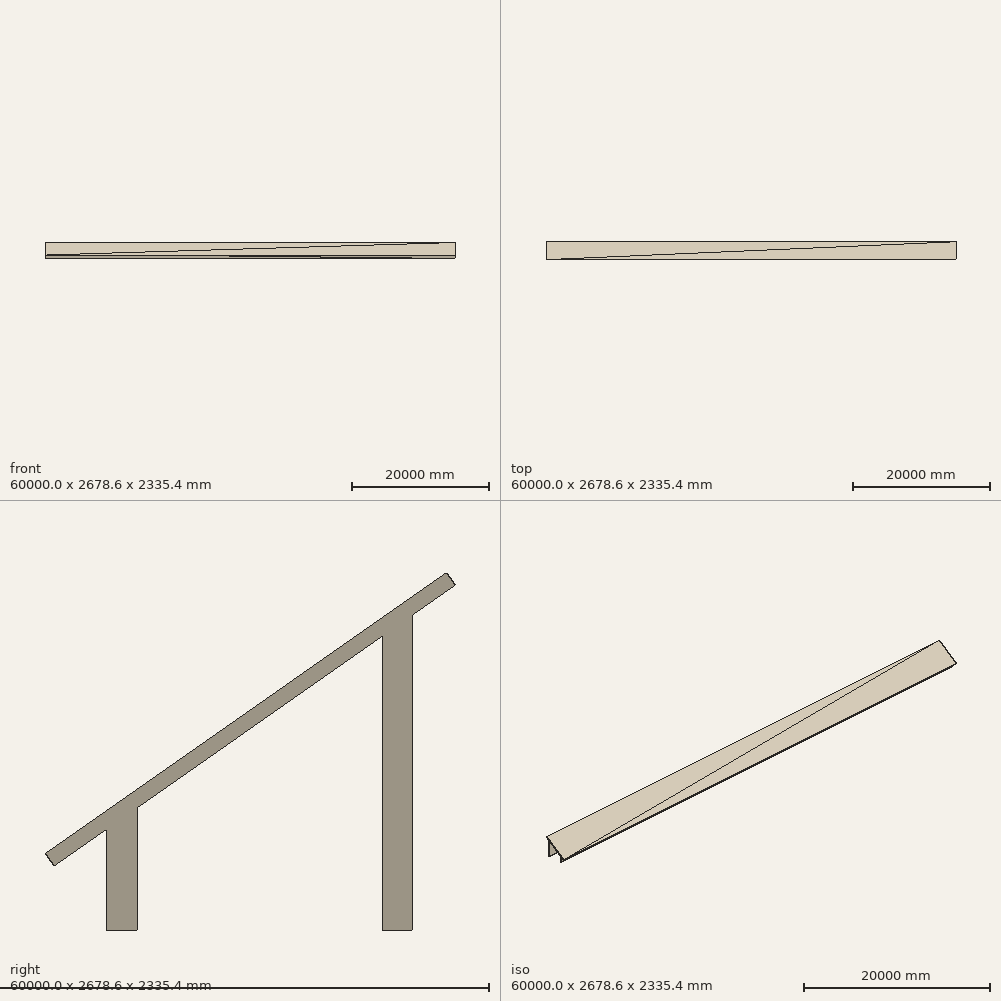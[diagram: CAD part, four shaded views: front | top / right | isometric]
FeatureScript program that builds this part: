
annotation { "Feature Type Name" : "Feature", "Feature Type Description" : "" }
export const myFeature = defineFeature(function(context is Context, id is Id, definition is map)
    precondition{}
    {
        {
            var Q0;
            Q0=qCreatedBy(makeId("Right.planeOp"),FACE);
            var sketch = newSketch(context, id + "F0", { "sketchPlane" : qUnion([Q0])});
            skLineSegment(sketch, "E0", {"start": v(0, 500) * mm, "end": v(2621.29, 2335.44) * mm});
            skLineSegment(sketch, "E1", {"start": v(0, 500) * mm, "end": v(57.36, 418.08) * mm});
            skLineSegment(sketch, "E2", {"start": v(57.36, 418.08) * mm, "end": v(400, 658) * mm});
            skLineSegment(sketch, "E3", {"start": v(400, 658) * mm, "end": v(400, 0) * mm});
            skLineSegment(sketch, "E4", {"start": v(400, 0) * mm, "end": v(600, 0) * mm});
            skLineSegment(sketch, "E5", {"start": v(600, 0) * mm, "end": v(600, 798.05) * mm});
            skLineSegment(sketch, "E6", {"start": v(600, 798.05) * mm, "end": v(2200, 1918.38) * mm});
            skLineSegment(sketch, "E7", {"start": v(2200, 1918.38) * mm, "end": v(2200, 0) * mm});
            skLineSegment(sketch, "E8", {"start": v(2200, 0) * mm, "end": v(2400, 0) * mm});
            skLineSegment(sketch, "E9", {"start": v(2400, 0) * mm, "end": v(2400, 2058.42) * mm});
            skLineSegment(sketch, "E10", {"start": v(2400, 2058.42) * mm, "end": v(2678.64, 2253.53) * mm});
            skLineSegment(sketch, "E11", {"start": v(2678.64, 2253.53) * mm, "end": v(2621.29, 2335.44) * mm});
            skSolve(sketch);
        }
        {
            var Q0;
            Q0 = qSketchRegion(id + "F0", true);
            extrude(context, id + "F1", {"entities" : qUnion([Q0]), "oppositeDirection" : true, "depth" : 60000 * mm, "offsetDistance" : 25 * mm});
        }
    });
